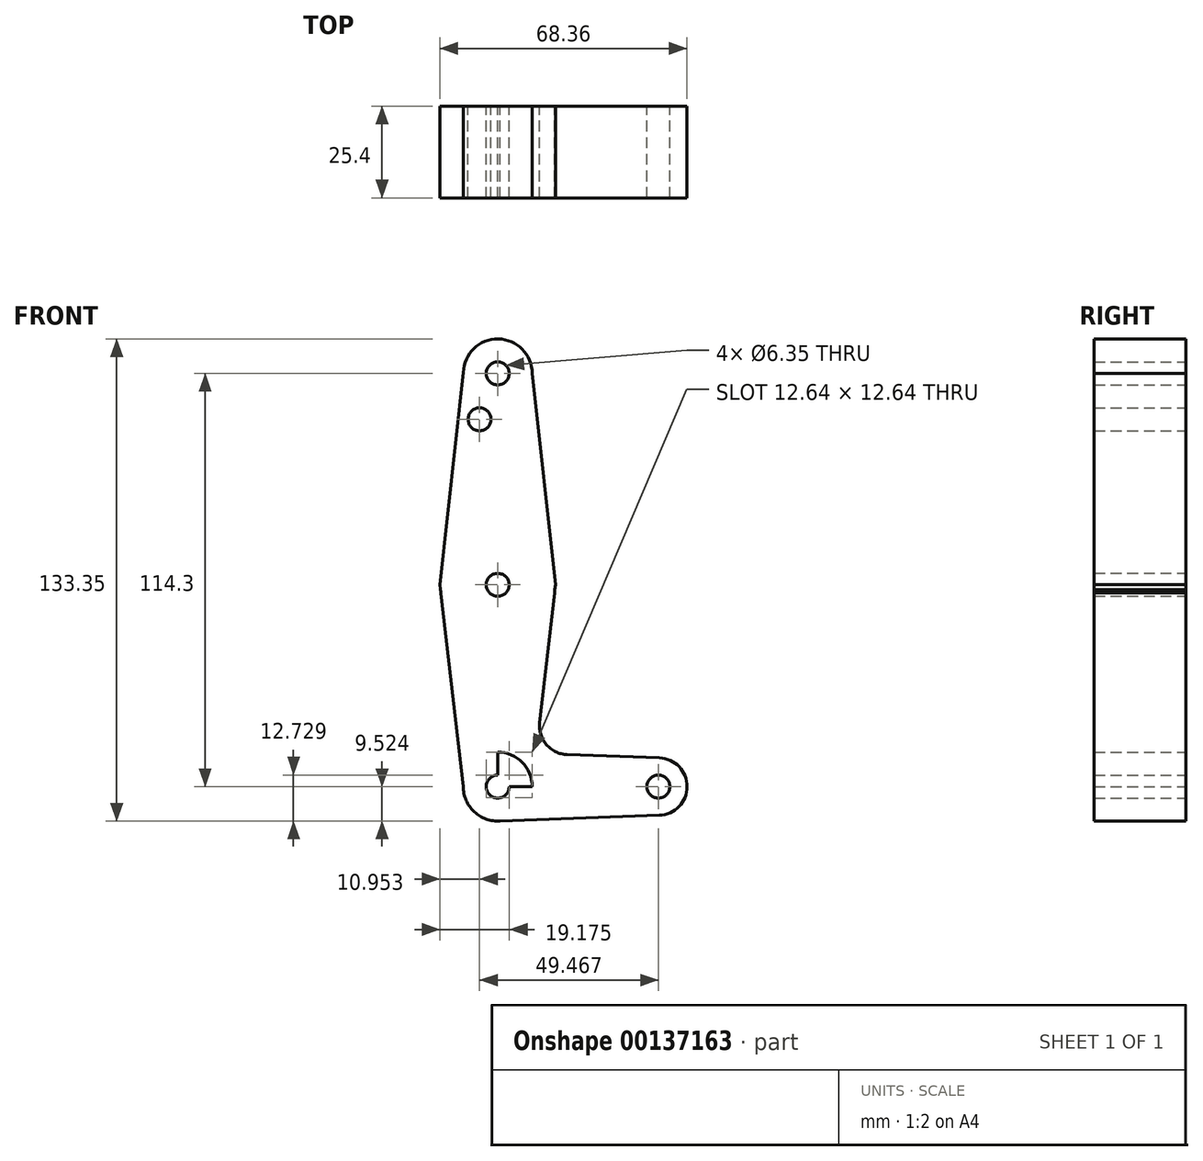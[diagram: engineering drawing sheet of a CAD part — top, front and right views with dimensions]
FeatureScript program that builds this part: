
annotation { "Feature Type Name" : "Feature", "Feature Type Description" : "" }
export const myFeature = defineFeature(function(context is Context, id is Id, definition is map)
    precondition{}
    {
        {
            var Q0;
            Q0=qCreatedBy(makeId("Front.planeOp"),FACE);
            var sketch = newSketch(context, id + "F0", { "sketchPlane" : qUnion([Q0])});
            skLineSegment(sketch, "E0", {"start": v(0, 58.48) * mm, "end": v(0, -55.82) * mm});
            skLineSegment(sketch, "E1", {"start": v(0, -55.82) * mm, "end": v(44.45, -55.82) * mm});
            skCircle(sketch, "E2", {"center": v(0, 0) * mm, "radius": 15.88 * mm});
            skCircle(sketch, "E3", {"center": v(0, 58.48) * mm, "radius": 9.53 * mm});
            skCircle(sketch, "E4", {"center": v(0, -55.82) * mm, "radius": 9.53 * mm});
            skCircle(sketch, "E5", {"center": v(44.45, -55.82) * mm, "radius": 7.94 * mm});
            skCircle(sketch, "E6", {"center": v(0, 58.48) * mm, "radius": 3.18 * mm});
            skCircle(sketch, "E7", {"center": v(0, 0) * mm, "radius": 3.18 * mm});
            skCircle(sketch, "E8", {"center": v(0, -55.82) * mm, "radius": 3.18 * mm});
            skCircle(sketch, "E9", {"center": v(44.45, -55.82) * mm, "radius": 3.18 * mm});
            skCircle(sketch, "E10", {"center": v(-5.02, 45.78) * mm, "radius": 3.18 * mm});
            skLineSegment(sketch, "E11", {"start": v(-9.52, 58.76) * mm, "end": v(-15.97, 0) * mm});
            skLineSegment(sketch, "E12", {"start": v(9.52, 58.48) * mm, "end": v(15.97, 0) * mm});
            skLineSegment(sketch, "E13", {"start": v(-9.52, -55.78) * mm, "end": v(-15.97, 0) * mm});
            skLineSegment(sketch, "E14", {"start": v(15.97, 0) * mm, "end": v(11.61, -38.13) * mm});
            skLineSegment(sketch, "E15", {"start": v(19.23, -46.98) * mm, "end": v(44.73, -47.88) * mm});
            skLineSegment(sketch, "E16", {"start": v(0, -65.34) * mm, "end": v(44.73, -63.75) * mm});
            skLineSegment(sketch, "E17", {"start": v(-123.34, 91.35) * mm, "end": v(-81.95, 103.9) * mm});
            skPoint(sketch, "E18.newPointA", {"position": v(0, -46.3) * mm});
            skArc(sketch, "E18.filletArc", {"start": v(11.61, -38.13) * mm, "mid": v(13.48, -44.22) * mm, "end": v(19.23, -46.98) * mm});
            skSolve(sketch);
        }
        {
            var Q0;
            Q0 = qSketchRegion(id + "F0", true);
            extrude(context, id + "F1", {"entities" : qUnion([Q0]), "depth" : 25.4 * mm});
        }
        {
            var Q0;
            Q0 = qSketchRegion(id + "F0", true);
            extrude(context, id + "F2", {"entities" : qUnion([Q0]), "operationType" : NewBodyOperationType.ADD, "depth" : 25.4 * mm});
        }
    });
